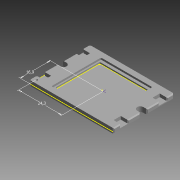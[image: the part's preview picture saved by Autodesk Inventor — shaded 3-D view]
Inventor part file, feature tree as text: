
AUTODESK INVENTOR PART (.ipt)
format: ipt  version: 2015 (Build 190159000, 159)  size: 293,376 bytes
history: native  units: in
note: dims shown in document units (in); Inventor stores cm internally (conversion verified against a paired STEP export)
features: sketch x8, extrude x6, chamfer x2, fillet x1
ambient origin geometry x8: Origin, YZ Plane, XZ Plane, XY Plane, X Axis, Y Axis, Z Axis, Center Point
bodies: Solid1 (feature_tree)
feature tree (17):
  extrude  "Extrusion1"  Depth=0.0689in TaperAngle=0.0deg
  extrude  "Extrusion2"  Depth=0.0394in
  extrude  "Extrusion3"  Depth=0.0394in
  chamfer  "Chamfer1"  Distance=0.1181in
  fillet  "Fillet1"  Radius=0.0079in
  chamfer  "Chamfer2"  Distance=0.0197in Angle=45.0deg
  extrude  "Extrusion4"  Depth=1.0709in
  extrude  "Extrusion5"  Depth=0.0709in TaperAngle=0.0deg
  extrude  "Extrusion6"  Depth=1.0945in
  sketch  "Sketch8"  dims[d64=1.1299in d66=1.0945in]
  sketch  "Sketch9"  dims[d67=0.0197in d68=0.0394in d69=0.0in d70=1.3661in d72=0.0276in d73=0.0in d74=0.9567in d75=0.6654in]
  sketch  "Sketch2"  dims[d33=0.1575in d34=0.1575in d35=0.1575in d36=1.3307in d37=0.1575in d38=0.1378in d39=0.0787in d40=0.1575in d41=1.8504in d42=0.0689in d43=0.0in]
  sketch  "Sketch3"  dims[d44=0.0394in d45=0.0in d46=0.0787in]
  sketch  "Sketch4"  dims[d47=0.0787in d48=0.0394in d49=0.1181in d50=0.0in]
  sketch  "Sketch5"  dims[d51=0.0197in d52=0.0787in d53=45.0deg d54=0.0079in d55=0.0197in d56=0.0787in d57=45.0deg]
  sketch  "Sketch6"  dims[d58=0.9764in d60=1.0709in]
  sketch  "Sketch7"  dims[d61=0.0197in d62=0.0709in d63=0.0in]
